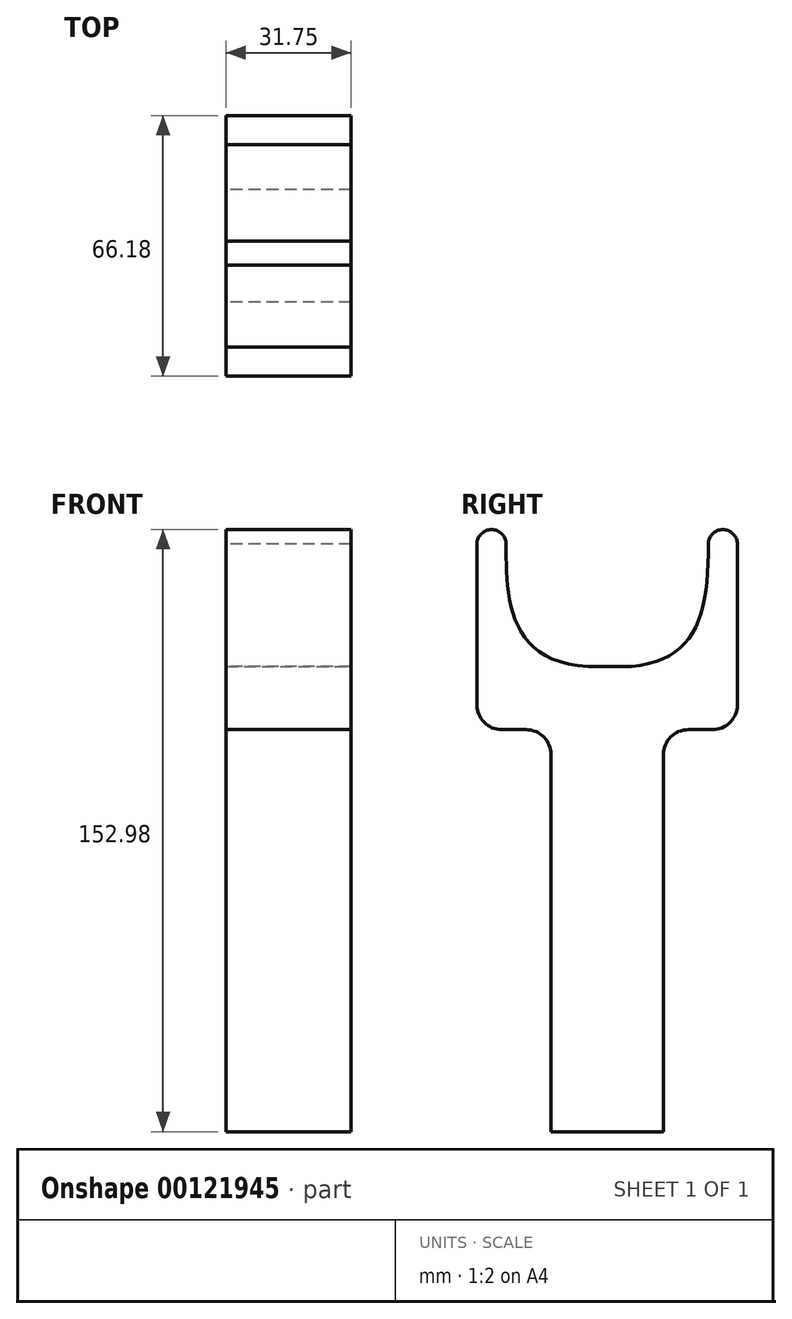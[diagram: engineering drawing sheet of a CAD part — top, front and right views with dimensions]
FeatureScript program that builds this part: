
annotation { "Feature Type Name" : "Feature", "Feature Type Description" : "" }
export const myFeature = defineFeature(function(context is Context, id is Id, definition is map)
    precondition{}
    {
        {
            var Q0;
            Q0=qCreatedBy(makeId("Right.planeOp"),FACE);
            var sketch = newSketch(context, id + "F0", { "sketchPlane" : qUnion([Q0])});
            skFitSpline(sketch, "E0", {"points": [v(-31.95, 44.64) * mm, v(-7.42, 75.73) * mm], "startDerivative": vector(61.61, -2.57) * mm, "endDerivative": vector(-0.86, 59.04) * mm});
            skPoint(sketch, "E1.start.orphan", {"position": v(0, 43.78) * mm});
            skLineSegment(sketch, "E2", {"start": v(-31.95, 44.64) * mm, "end": v(-38.03, 44.64) * mm});
            skFitSpline(sketch, "E3", {"points": [v(-58.76, 75.73) * mm, v(-38.03, 44.64) * mm], "startDerivative": vector(0, -38.5) * mm, "endDerivative": vector(62.2, -3.42) * mm});
            skLineSegment(sketch, "E4", {"start": v(-66.18, 75.73) * mm, "end": v(-66.18, 34.94) * mm});
            skLineSegment(sketch, "E5", {"start": v(-59.83, 28.59) * mm, "end": v(-53.7, 28.59) * mm});
            skLineSegment(sketch, "E6", {"start": v(-47.35, 22.24) * mm, "end": v(-47.35, -73.54) * mm});
            skLineSegment(sketch, "E7", {"start": v(0, 75.73) * mm, "end": v(0, 34.94) * mm});
            skLineSegment(sketch, "E8", {"start": v(-6.35, 28.59) * mm, "end": v(-12.48, 28.59) * mm});
            skLineSegment(sketch, "E9", {"start": v(-18.83, 22.24) * mm, "end": v(-18.83, -73.54) * mm});
            skLineSegment(sketch, "E10", {"start": v(-47.35, -73.54) * mm, "end": v(-18.83, -73.54) * mm});
            skPoint(sketch, "E11.visualSharp", {"position": v(-66.18, 28.59) * mm});
            skArc(sketch, "E11.filletArc", {"start": v(-66.18, 34.94) * mm, "mid": v(-64.32, 30.45) * mm, "end": v(-59.83, 28.59) * mm});
            skPoint(sketch, "E12.visualSharp", {"position": v(0, 28.59) * mm});
            skArc(sketch, "E12.filletArc", {"start": v(-6.35, 28.59) * mm, "mid": v(-1.86, 30.45) * mm, "end": v(0, 34.94) * mm});
            skArc(sketch, "E13", {"start": v(-58.76, 75.73) * mm, "mid": v(-62.47, 79.44) * mm, "end": v(-66.18, 75.73) * mm});
            skArc(sketch, "E14", {"start": v(0, 75.73) * mm, "mid": v(-3.7, 79.44) * mm, "end": v(-7.42, 75.73) * mm});
            skPoint(sketch, "E15.visualSharp", {"position": v(-47.35, 28.59) * mm});
            skArc(sketch, "E15.filletArc", {"start": v(-47.35, 22.24) * mm, "mid": v(-49.2, 26.73) * mm, "end": v(-53.7, 28.59) * mm});
            skPoint(sketch, "E16.visualSharp", {"position": v(-18.83, 28.59) * mm});
            skArc(sketch, "E16.filletArc", {"start": v(-12.48, 28.59) * mm, "mid": v(-16.97, 26.73) * mm, "end": v(-18.83, 22.24) * mm});
            skSolve(sketch);
        }
        {
            var Q0;
            Q0 = qSketchRegion(id + "F0", true);
            extrude(context, id + "F1", {"entities" : qUnion([Q0]), "depth" : 31.75 * mm});
        }
    });
